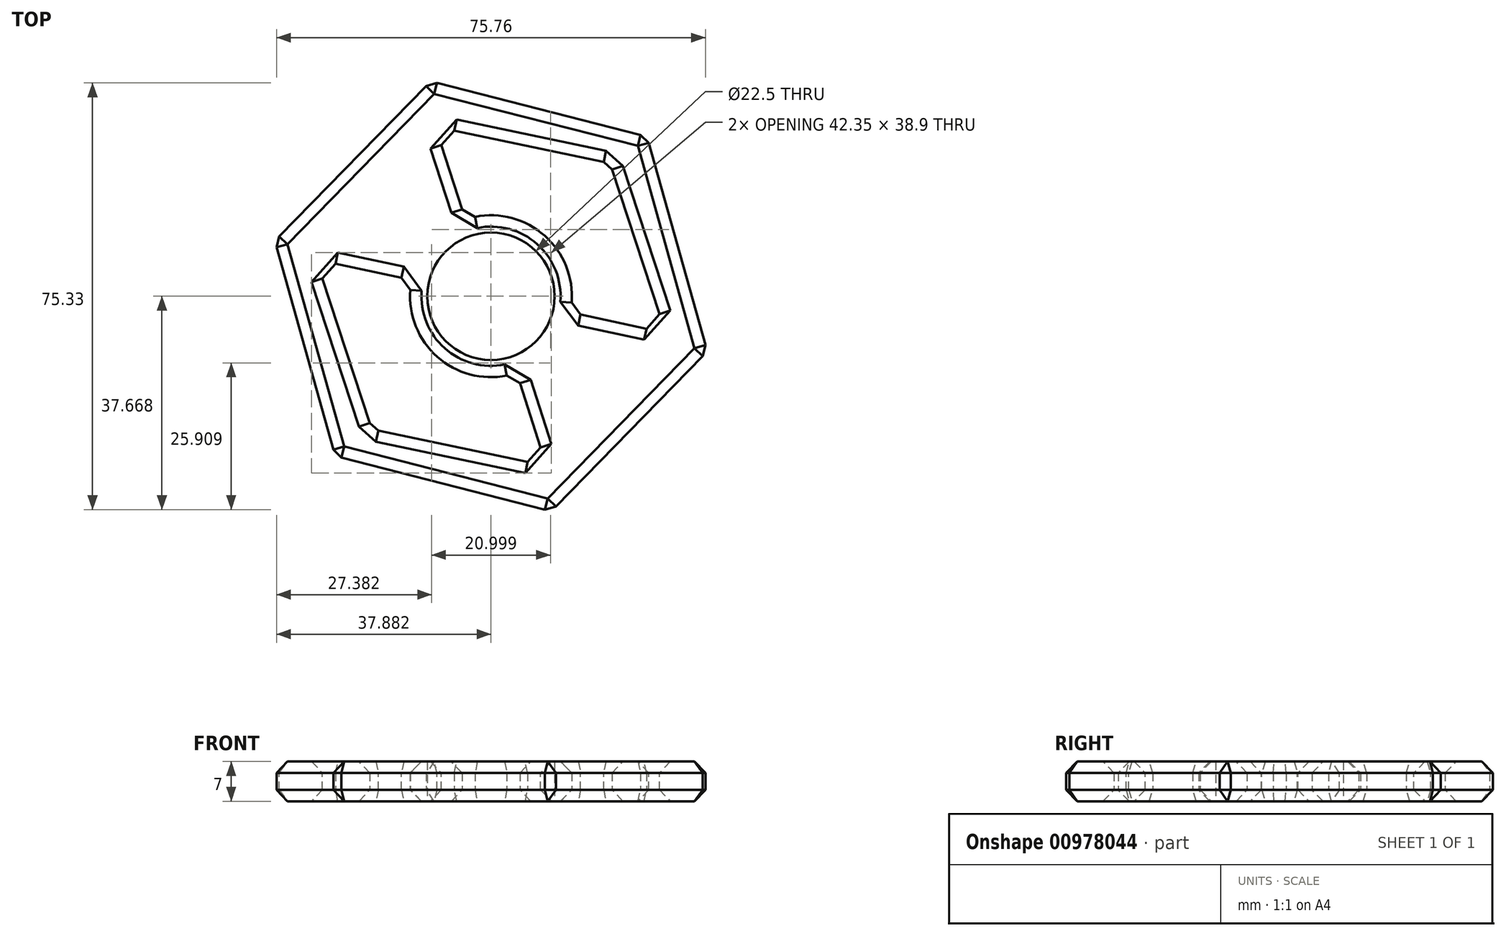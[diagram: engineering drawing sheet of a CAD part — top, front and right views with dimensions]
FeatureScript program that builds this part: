
annotation { "Feature Type Name" : "Feature", "Feature Type Description" : "" }
export const myFeature = defineFeature(function(context is Context, id is Id, definition is map)
    precondition{}
    {
        {
            var Q0;
            Q0=qCreatedBy(makeId("Top.planeOp"),FACE);
            var sketch = newSketch(context, id + "F0", { "sketchPlane" : qUnion([Q0])});
            skCircle(sketch, "E0.cCircle", {"center": v(-24.83, -4.84) * mm, "radius": 34.14 * mm, "construction": true});
            skLineSegment(sketch, "E0.0", {"start": v(2.72, 23.36) * mm, "end": v(13.36, -14.6) * mm});
            skLineSegment(sketch, "E0.1", {"start": v(13.36, -14.6) * mm, "end": v(-14.18, -42.8) * mm});
            skLineSegment(sketch, "E0.2", {"start": v(-14.18, -42.8) * mm, "end": v(-52.37, -33.04) * mm});
            skLineSegment(sketch, "E0.3", {"start": v(-52.37, -33.04) * mm, "end": v(-63.02, 4.91) * mm});
            skLineSegment(sketch, "E0.4", {"start": v(-63.02, 4.91) * mm, "end": v(-35.48, 33.11) * mm});
            skLineSegment(sketch, "E0.5", {"start": v(-35.48, 33.11) * mm, "end": v(2.72, 23.36) * mm});
            skPoint(sketch, "E0.0.midPoint", {"position": v(8.04, 4.38) * mm});
            skCircle(sketch, "E1", {"center": v(-24.83, -4.84) * mm, "radius": 11.25 * mm});
            skCircle(sketch, "E2.cCircle", {"center": v(-24.83, -4.84) * mm, "radius": 27.3 * mm, "construction": true});
            skLineSegment(sketch, "E2.0", {"start": v(-3.8, 18.65) * mm, "end": v(6.03, -11.3) * mm});
            skLineSegment(sketch, "E2.1", {"start": v(6.03, -11.3) * mm, "end": v(-15, -34.8) * mm});
            skLineSegment(sketch, "E2.2", {"start": v(-15, -34.8) * mm, "end": v(-45.85, -28.34) * mm});
            skLineSegment(sketch, "E2.3", {"start": v(-45.85, -28.34) * mm, "end": v(-55.69, 1.62) * mm});
            skLineSegment(sketch, "E2.4", {"start": v(-55.69, 1.62) * mm, "end": v(-34.66, 25.12) * mm});
            skLineSegment(sketch, "E2.5", {"start": v(-34.66, 25.12) * mm, "end": v(-3.8, 18.65) * mm});
            skPoint(sketch, "E2.0.midPoint", {"position": v(1.12, 3.67) * mm});
            skLineSegment(sketch, "E3", {"start": v(-34.66, 25.12) * mm, "end": v(-28.42, 5.82) * mm});
            skLineSegment(sketch, "E4.1.0", {"start": v(-55.69, 1.62) * mm, "end": v(-35.86, -2.62) * mm});
            skLineSegment(sketch, "E4.2.0", {"start": v(-45.85, -28.34) * mm, "end": v(-32.26, -13.28) * mm});
            skLineSegment(sketch, "E4.3.0", {"start": v(-15, -34.8) * mm, "end": v(-21.24, -15.5) * mm});
            skLineSegment(sketch, "E4.4.0", {"start": v(6.03, -11.3) * mm, "end": v(-13.8, -7.06) * mm});
            skLineSegment(sketch, "E4.5.0", {"start": v(-3.8, 18.65) * mm, "end": v(-17.4, 3.6) * mm});
            skCircle(sketch, "E5", {"center": v(-24.83, -4.84) * mm, "radius": 14.3 * mm});
            skSolve(sketch);
        }
        {
            var Q0;
            Q0=makeQuery(id+"F0.imprint","IMPRINT",FACE,{"disambiguationData":[TD([[makeQuery(id+"F0.imprint","IMPRINT",EDGE,{"derivedFrom":sQuery(id+"F0.wireOp",EDGE,"E0.0")}),-1.0]])]});
            var Q1;
            Q1=makeQuery(id+"F0.imprint","IMPRINT",FACE,{"disambiguationData":[TD([[makeQuery(id+"F0.imprint","IMPRINT",EDGE,{"derivedFrom":sQuery(id+"F0.wireOp",EDGE,"E2.4")}),-1.0]])]});
            var Q2;
            Q2=makeQuery(id+"F0.imprint","IMPRINT",FACE,{"disambiguationData":[TD([[makeQuery(id+"F0.imprint","IMPRINT",EDGE,{"derivedFrom":sQuery(id+"F0.wireOp",EDGE,"E2.1")}),-1.0]])]});
            var Q3;
            {var subQ0=sQuery(id+"F0.wireOp",EDGE,"E3");var subQ1=sQuery(id+"F0.wireOp",EDGE,"E1");var subQ2=makeQuery(id+"F0.imprint","INTERSECT",VERTEX,{"derivedFrom":[subQ1,subQ0]});Q3=makeQuery(id+"F0.imprint","IMPRINT",FACE,{"disambiguationData":[TD([[makeQuery(id+"F0.imprint","IMPRINT",EDGE,{"disambiguationData":[TD([[subQ2,-1.0]])],"derivedFrom":subQ1}),-1.0]])]});}
            var Q4;
            {var subQ0=sQuery(id+"F0.wireOp",EDGE,"E4.3.0");var subQ1=sQuery(id+"F0.wireOp",EDGE,"E1");var subQ2=makeQuery(id+"F0.imprint","INTERSECT",VERTEX,{"derivedFrom":[subQ1,subQ0]});Q4=makeQuery(id+"F0.imprint","IMPRINT",FACE,{"disambiguationData":[TD([[makeQuery(id+"F0.imprint","IMPRINT",EDGE,{"disambiguationData":[TD([[subQ2,-1.0]])],"derivedFrom":subQ1}),-1.0]])]});}
            var Q5;
            {var subQ0=sQuery(id+"F0.wireOp",EDGE,"E4.2.0");var subQ1=sQuery(id+"F0.wireOp",EDGE,"E1");var subQ2=makeQuery(id+"F0.imprint","INTERSECT",VERTEX,{"derivedFrom":[subQ1,subQ0]});Q5=makeQuery(id+"F0.imprint","IMPRINT",FACE,{"disambiguationData":[TD([[makeQuery(id+"F0.imprint","IMPRINT",EDGE,{"disambiguationData":[TD([[subQ2,-1.0]])],"derivedFrom":subQ1}),-1.0]])]});}
            var Q6;
            {var subQ0=sQuery(id+"F0.wireOp",EDGE,"E4.1.0");var subQ1=sQuery(id+"F0.wireOp",EDGE,"E1");var subQ2=makeQuery(id+"F0.imprint","INTERSECT",VERTEX,{"derivedFrom":[subQ1,subQ0]});Q6=makeQuery(id+"F0.imprint","IMPRINT",FACE,{"disambiguationData":[TD([[makeQuery(id+"F0.imprint","IMPRINT",EDGE,{"disambiguationData":[TD([[subQ2,-1.0]])],"derivedFrom":subQ1}),-1.0]])]});}
            var Q7;
            {var subQ0=sQuery(id+"F0.wireOp",EDGE,"E3");var subQ1=sQuery(id+"F0.wireOp",EDGE,"E1");var subQ2=makeQuery(id+"F0.imprint","INTERSECT",VERTEX,{"derivedFrom":[subQ1,subQ0]});Q7=makeQuery(id+"F0.imprint","IMPRINT",FACE,{"disambiguationData":[TD([[makeQuery(id+"F0.imprint","IMPRINT",EDGE,{"disambiguationData":[TD([[subQ2,1.0]])],"derivedFrom":subQ1}),-1.0]])]});}
            var Q8;
            {var subQ0=sQuery(id+"F0.wireOp",EDGE,"E4.4.0");var subQ1=sQuery(id+"F0.wireOp",EDGE,"E1");var subQ2=makeQuery(id+"F0.imprint","INTERSECT",VERTEX,{"derivedFrom":[subQ1,subQ0]});Q8=makeQuery(id+"F0.imprint","IMPRINT",FACE,{"disambiguationData":[TD([[makeQuery(id+"F0.imprint","IMPRINT",EDGE,{"disambiguationData":[TD([[subQ2,-1.0]])],"derivedFrom":subQ1}),-1.0]])]});}
            extrude(context, id + "F1", {"entities" : qUnion([Q0, Q1, Q2, Q3, Q4, Q5, Q6, Q7, Q8]), "depth" : 7 * mm, "offsetDistance" : 25 * mm});
        }
        {
            var Q0;
            Q0=makeQuery(id+"F1.opExtrude","CAP_EDGE",EDGE,{"disambiguationData":[OSD([sQuery(id+"F0.wireOp",EDGE,"E0.4")])],"isStart":false});
            var Q1;
            Q1=makeQuery(id+"F1.opExtrude","CAP_EDGE",EDGE,{"disambiguationData":[OSD([sQuery(id+"F0.wireOp",EDGE,"E0.1")])],"isStart":false});
            var Q2;
            {var subQ0=sQuery(id+"F0.wireOp",EDGE,"E5");var subQ1=makeQuery(id+"F0.imprint","INTERSECT",VERTEX,{"derivedFrom":[sQuery(id+"F0.wireOp",EDGE,"E4.2.0"),subQ0]});Q2=makeQuery(id+"F1.opExtrude","CAP_EDGE",EDGE,{"disambiguationData":[OSD([subQ0]),TDD([makeQuery(id+"F0.imprint","IMPRINT",EDGE,{"disambiguationData":[TD([[makeQuery(id+"F0.imprint","INTERSECT",VERTEX,{"derivedFrom":[sQuery(id+"F0.wireOp",EDGE,"E4.1.0"),subQ0]}),-1.0]])],"derivedFrom":subQ0}),makeQuery(id+"F0.imprint","IMPRINT",EDGE,{"disambiguationData":[TD([[subQ1,-1.0]])],"derivedFrom":subQ0})])],"isStart":false});}
            var Q3;
            Q3=makeQuery(id+"F1.opExtrude","CAP_EDGE",EDGE,{"disambiguationData":[OSD([sQuery(id+"F0.wireOp",EDGE,"E4.1.0")])],"isStart":false});
            var Q4;
            Q4=makeQuery(id+"F1.opExtrude","SWEPT_EDGE",EDGE,{"disambiguationData":[OSD([sQuery(id+"F0.wireOp",EDGE,"E0.4"),sQuery(id+"F0.wireOp",EDGE,"E0.5")])]});
            var Q5;
            Q5=makeQuery(id+"F1.opExtrude","CAP_EDGE",EDGE,{"disambiguationData":[OSD([sQuery(id+"F0.wireOp",EDGE,"E4.3.0")])],"isStart":false});
            var Q6;
            Q6=makeQuery(id+"F1.opExtrude","CAP_EDGE",EDGE,{"disambiguationData":[OSD([sQuery(id+"F0.wireOp",EDGE,"E0.1")])],"isStart":true});
            var Q7;
            {var subQ0=sQuery(id+"F0.wireOp",EDGE,"E5");Q7=makeQuery(id+"F1.opExtrude","CAP_EDGE",EDGE,{"disambiguationData":[OSD([subQ0]),TDD([makeQuery(id+"F0.imprint","IMPRINT",EDGE,{"disambiguationData":[TD([[makeQuery(id+"F0.imprint","INTERSECT",VERTEX,{"derivedFrom":[sQuery(id+"F0.wireOp",EDGE,"E3"),subQ0]}),1.0]])],"derivedFrom":subQ0}),makeQuery(id+"F0.imprint","IMPRINT",EDGE,{"disambiguationData":[TD([[makeQuery(id+"F0.imprint","INTERSECT",VERTEX,{"derivedFrom":[sQuery(id+"F0.wireOp",EDGE,"E4.4.0"),subQ0]}),-1.0]])],"derivedFrom":subQ0})])],"isStart":true});}
            var Q8;
            {var subQ0=sQuery(id+"F0.wireOp",EDGE,"E5");Q8=makeQuery(id+"F1.opExtrude","CAP_EDGE",EDGE,{"disambiguationData":[OSD([subQ0]),TDD([makeQuery(id+"F0.imprint","IMPRINT",EDGE,{"disambiguationData":[TD([[makeQuery(id+"F0.imprint","INTERSECT",VERTEX,{"derivedFrom":[sQuery(id+"F0.wireOp",EDGE,"E3"),subQ0]}),1.0]])],"derivedFrom":subQ0}),makeQuery(id+"F0.imprint","IMPRINT",EDGE,{"disambiguationData":[TD([[makeQuery(id+"F0.imprint","INTERSECT",VERTEX,{"derivedFrom":[sQuery(id+"F0.wireOp",EDGE,"E4.4.0"),subQ0]}),-1.0]])],"derivedFrom":subQ0})])],"isStart":false});}
            var Q9;
            Q9=makeQuery(id+"F1.opExtrude","CAP_EDGE",EDGE,{"disambiguationData":[OSD([sQuery(id+"F0.wireOp",EDGE,"E4.4.0")])],"isStart":false});
            var Q10;
            Q10=makeQuery(id+"F1.opExtrude","CAP_EDGE",EDGE,{"disambiguationData":[OSD([sQuery(id+"F0.wireOp",EDGE,"E4.4.0")])],"isStart":true});
            var Q11;
            Q11=makeQuery(id+"F1.opExtrude","CAP_EDGE",EDGE,{"disambiguationData":[OSD([sQuery(id+"F0.wireOp",EDGE,"E4.1.0")])],"isStart":true});
            var Q12;
            Q12=makeQuery(id+"F1.opExtrude","CAP_EDGE",EDGE,{"disambiguationData":[OSD([sQuery(id+"F0.wireOp",EDGE,"E2.5")])],"isStart":true});
            var Q13;
            Q13=makeQuery(id+"F1.opExtrude","SWEPT_EDGE",EDGE,{"disambiguationData":[OSD([sQuery(id+"F0.wireOp",EDGE,"E4.1.0"),sQuery(id+"F0.wireOp",EDGE,"E5")])]});
            var Q14;
            Q14=makeQuery(id+"F1.opExtrude","SWEPT_EDGE",EDGE,{"disambiguationData":[OSD([sQuery(id+"F0.wireOp",EDGE,"E2.1"),sQuery(id+"F0.wireOp",EDGE,"E2.2"),sQuery(id+"F0.wireOp",EDGE,"E4.3.0")])]});
            var Q15;
            Q15=makeQuery(id+"F1.opExtrude","SWEPT_EDGE",EDGE,{"disambiguationData":[OSD([sQuery(id+"F0.wireOp",EDGE,"E0.0"),sQuery(id+"F0.wireOp",EDGE,"E0.1")])]});
            var Q16;
            Q16=makeQuery(id+"F1.opExtrude","SWEPT_EDGE",EDGE,{"disambiguationData":[OSD([sQuery(id+"F0.wireOp",EDGE,"E2.0"),sQuery(id+"F0.wireOp",EDGE,"E2.1"),sQuery(id+"F0.wireOp",EDGE,"E4.4.0")])]});
            var Q17;
            Q17=makeQuery(id+"F1.opExtrude","CAP_EDGE",EDGE,{"disambiguationData":[OSD([sQuery(id+"F0.wireOp",EDGE,"E2.0")])],"isStart":false});
            var Q18;
            Q18=makeQuery(id+"F1.opExtrude","CAP_EDGE",EDGE,{"disambiguationData":[OSD([sQuery(id+"F0.wireOp",EDGE,"E2.0")])],"isStart":true});
            var Q19;
            Q19=makeQuery(id+"F1.opExtrude","CAP_EDGE",EDGE,{"disambiguationData":[OSD([sQuery(id+"F0.wireOp",EDGE,"E3")])],"isStart":false});
            var Q20;
            Q20=makeQuery(id+"F1.opExtrude","SWEPT_EDGE",EDGE,{"disambiguationData":[OSD([sQuery(id+"F0.wireOp",EDGE,"E2.0"),sQuery(id+"F0.wireOp",EDGE,"E2.5"),sQuery(id+"F0.wireOp",EDGE,"E4.5.0")])]});
            var Q21;
            Q21=makeQuery(id+"F1.opExtrude","SWEPT_EDGE",EDGE,{"disambiguationData":[OSD([sQuery(id+"F0.wireOp",EDGE,"E0.1"),sQuery(id+"F0.wireOp",EDGE,"E0.2")])]});
            var Q22;
            {var subQ0=sQuery(id+"F0.wireOp",EDGE,"E5");var subQ1=makeQuery(id+"F0.imprint","INTERSECT",VERTEX,{"derivedFrom":[sQuery(id+"F0.wireOp",EDGE,"E4.2.0"),subQ0]});Q22=makeQuery(id+"F1.opExtrude","CAP_EDGE",EDGE,{"disambiguationData":[OSD([subQ0]),TDD([makeQuery(id+"F0.imprint","IMPRINT",EDGE,{"disambiguationData":[TD([[makeQuery(id+"F0.imprint","INTERSECT",VERTEX,{"derivedFrom":[sQuery(id+"F0.wireOp",EDGE,"E4.1.0"),subQ0]}),-1.0]])],"derivedFrom":subQ0}),makeQuery(id+"F0.imprint","IMPRINT",EDGE,{"disambiguationData":[TD([[subQ1,-1.0]])],"derivedFrom":subQ0})])],"isStart":true});}
            var Q23;
            Q23=makeQuery(id+"F1.opExtrude","SWEPT_EDGE",EDGE,{"disambiguationData":[OSD([sQuery(id+"F0.wireOp",EDGE,"E2.3"),sQuery(id+"F0.wireOp",EDGE,"E2.4"),sQuery(id+"F0.wireOp",EDGE,"E4.1.0")])]});
            var Q24;
            Q24=makeQuery(id+"F1.opExtrude","CAP_EDGE",EDGE,{"disambiguationData":[OSD([sQuery(id+"F0.wireOp",EDGE,"E4.3.0")])],"isStart":true});
            var Q25;
            Q25=makeQuery(id+"F1.opExtrude","CAP_EDGE",EDGE,{"disambiguationData":[OSD([sQuery(id+"F0.wireOp",EDGE,"E3")])],"isStart":true});
            var Q26;
            Q26=makeQuery(id+"F1.opExtrude","SWEPT_EDGE",EDGE,{"disambiguationData":[OSD([sQuery(id+"F0.wireOp",EDGE,"E2.4"),sQuery(id+"F0.wireOp",EDGE,"E2.5"),sQuery(id+"F0.wireOp",EDGE,"E3")])]});
            var Q27;
            Q27=makeQuery(id+"F1.opExtrude","CAP_EDGE",EDGE,{"disambiguationData":[OSD([sQuery(id+"F0.wireOp",EDGE,"E2.5")])],"isStart":false});
            var Q28;
            Q28=makeQuery(id+"F1.opExtrude","SWEPT_EDGE",EDGE,{"disambiguationData":[OSD([sQuery(id+"F0.wireOp",EDGE,"E3"),sQuery(id+"F0.wireOp",EDGE,"E5")])]});
            var Q29;
            Q29=makeQuery(id+"F1.opExtrude","SWEPT_EDGE",EDGE,{"disambiguationData":[OSD([sQuery(id+"F0.wireOp",EDGE,"E4.3.0"),sQuery(id+"F0.wireOp",EDGE,"E5")])]});
            var Q30;
            Q30=makeQuery(id+"F1.opExtrude","SWEPT_EDGE",EDGE,{"disambiguationData":[OSD([sQuery(id+"F0.wireOp",EDGE,"E4.4.0"),sQuery(id+"F0.wireOp",EDGE,"E5")])]});
            var Q31;
            Q31=makeQuery(id+"F1.opExtrude","CAP_EDGE",EDGE,{"disambiguationData":[OSD([sQuery(id+"F0.wireOp",EDGE,"E0.3")])],"isStart":true});
            var Q32;
            Q32=makeQuery(id+"F1.opExtrude","CAP_EDGE",EDGE,{"disambiguationData":[OSD([sQuery(id+"F0.wireOp",EDGE,"E0.2")])],"isStart":false});
            var Q33;
            Q33=makeQuery(id+"F1.opExtrude","CAP_EDGE",EDGE,{"disambiguationData":[OSD([sQuery(id+"F0.wireOp",EDGE,"E0.3")])],"isStart":false});
            var Q34;
            Q34=makeQuery(id+"F1.opExtrude","CAP_EDGE",EDGE,{"disambiguationData":[OSD([sQuery(id+"F0.wireOp",EDGE,"E2.2")])],"isStart":false});
            var Q35;
            Q35=makeQuery(id+"F1.opExtrude","CAP_EDGE",EDGE,{"disambiguationData":[OSD([sQuery(id+"F0.wireOp",EDGE,"E0.2")])],"isStart":true});
            var Q36;
            Q36=makeQuery(id+"F1.opExtrude","CAP_EDGE",EDGE,{"disambiguationData":[OSD([sQuery(id+"F0.wireOp",EDGE,"E0.4")])],"isStart":true});
            var Q37;
            Q37=makeQuery(id+"F1.opExtrude","CAP_EDGE",EDGE,{"disambiguationData":[OSD([sQuery(id+"F0.wireOp",EDGE,"E2.3")])],"isStart":false});
            var Q38;
            Q38=makeQuery(id+"F1.opExtrude","CAP_EDGE",EDGE,{"disambiguationData":[OSD([sQuery(id+"F0.wireOp",EDGE,"E0.0")])],"isStart":false});
            var Q39;
            Q39=makeQuery(id+"F1.opExtrude","CAP_EDGE",EDGE,{"disambiguationData":[OSD([sQuery(id+"F0.wireOp",EDGE,"E0.5")])],"isStart":false});
            var Q40;
            Q40=makeQuery(id+"F1.opExtrude","CAP_EDGE",EDGE,{"disambiguationData":[OSD([sQuery(id+"F0.wireOp",EDGE,"E0.0")])],"isStart":true});
            var Q41;
            Q41=makeQuery(id+"F1.opExtrude","CAP_EDGE",EDGE,{"disambiguationData":[OSD([sQuery(id+"F0.wireOp",EDGE,"E0.5")])],"isStart":true});
            var Q42;
            Q42=makeQuery(id+"F1.opExtrude","SWEPT_EDGE",EDGE,{"disambiguationData":[OSD([sQuery(id+"F0.wireOp",EDGE,"E2.2"),sQuery(id+"F0.wireOp",EDGE,"E2.3"),sQuery(id+"F0.wireOp",EDGE,"E4.2.0")])]});
            var Q43;
            Q43=makeQuery(id+"F1.opExtrude","CAP_EDGE",EDGE,{"disambiguationData":[OSD([sQuery(id+"F0.wireOp",EDGE,"E2.2")])],"isStart":true});
            var Q44;
            Q44=makeQuery(id+"F1.opExtrude","SWEPT_EDGE",EDGE,{"disambiguationData":[OSD([sQuery(id+"F0.wireOp",EDGE,"E0.0"),sQuery(id+"F0.wireOp",EDGE,"E0.5")])]});
            var Q45;
            Q45=makeQuery(id+"F1.opExtrude","SWEPT_EDGE",EDGE,{"disambiguationData":[OSD([sQuery(id+"F0.wireOp",EDGE,"E0.2"),sQuery(id+"F0.wireOp",EDGE,"E0.3")])]});
            var Q46;
            Q46=makeQuery(id+"F1.opExtrude","SWEPT_EDGE",EDGE,{"disambiguationData":[OSD([sQuery(id+"F0.wireOp",EDGE,"E0.3"),sQuery(id+"F0.wireOp",EDGE,"E0.4")])]});
            var Q47;
            Q47=makeQuery(id+"F1.opExtrude","CAP_EDGE",EDGE,{"disambiguationData":[OSD([sQuery(id+"F0.wireOp",EDGE,"E2.3")])],"isStart":true});
            chamfer(context, id + "F2", {"entities" : qUnion([Q0, Q1, Q2, Q3, Q4, Q5, Q6, Q7, Q8, Q9, Q10, Q11, Q12, Q13, Q14, Q15, Q16, Q17, Q18, Q19, Q20, Q21, Q22, Q23, Q24, Q25, Q26, Q27, Q28, Q29, Q30, Q31, Q32, Q33, Q34, Q35, Q36, Q37, Q38, Q39, Q40, Q41, Q42, Q43, Q44, Q45, Q46, Q47]), "width" : 2 * mm, "tangentPropagation" : true});
        }
    });
